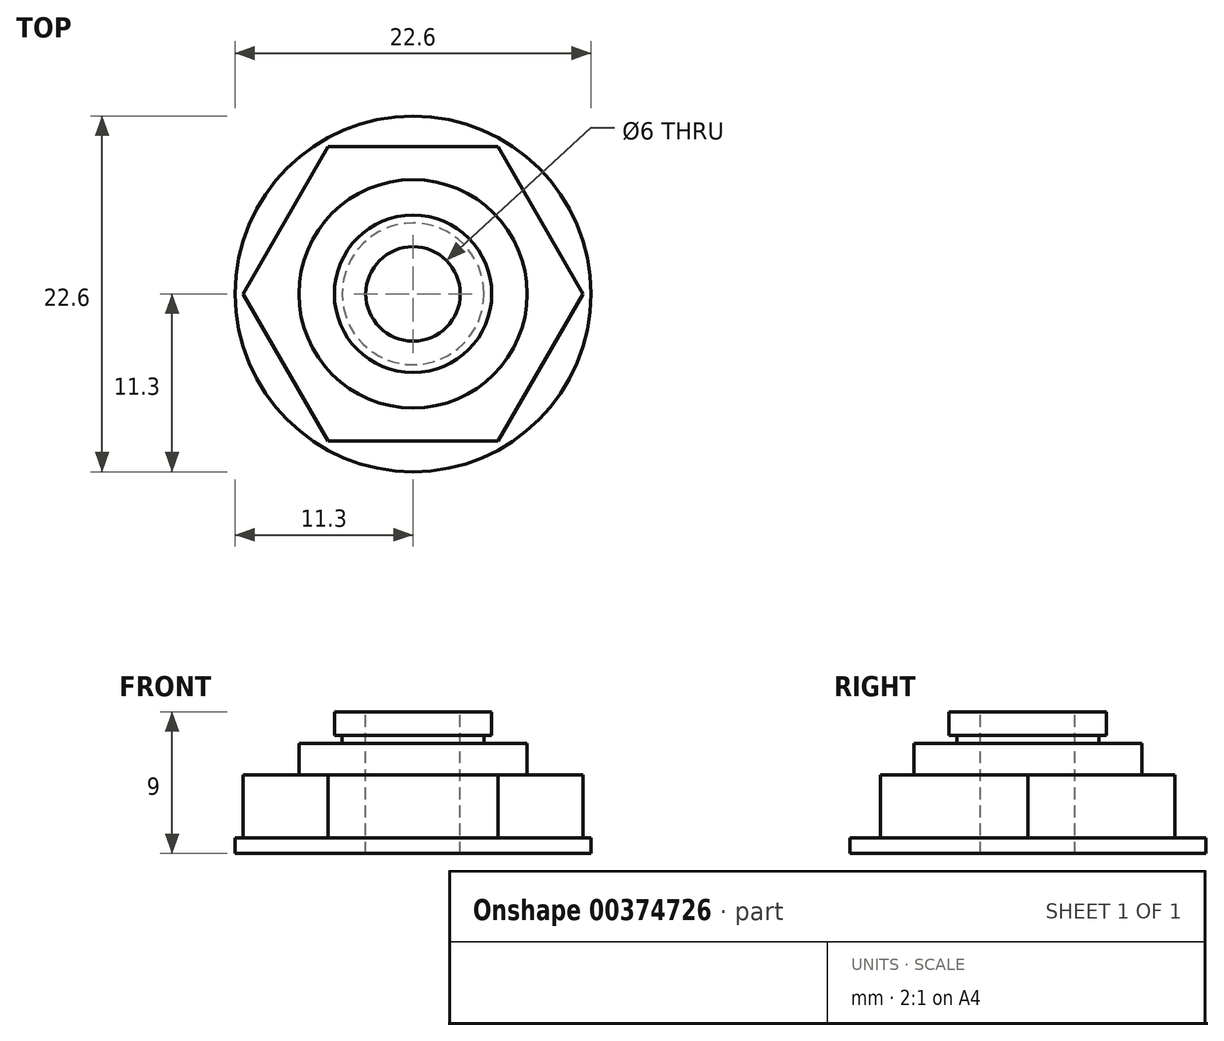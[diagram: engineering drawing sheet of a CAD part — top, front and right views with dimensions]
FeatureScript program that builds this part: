
annotation { "Feature Type Name" : "Feature", "Feature Type Description" : "" }
export const myFeature = defineFeature(function(context is Context, id is Id, definition is map)
    precondition{}
    {
        {
            var Q0;
            Q0=qCreatedBy(makeId("Top.planeOp"),FACE);
            var sketch = newSketch(context, id + "F0", { "sketchPlane" : qUnion([Q0])});
            skCircle(sketch, "E0", {"center": v(0, 0) * mm, "radius": 11.3 * mm});
            skCircle(sketch, "E1.cCircle", {"center": v(0, 0) * mm, "radius": 10.8 * mm, "construction": true});
            skLineSegment(sketch, "E1.0", {"start": v(5.4, -9.35) * mm, "end": v(-5.4, -9.35) * mm});
            skLineSegment(sketch, "E1.1", {"start": v(-5.4, -9.35) * mm, "end": v(-10.8, 0) * mm});
            skLineSegment(sketch, "E1.2", {"start": v(-10.8, 0) * mm, "end": v(-5.4, 9.35) * mm});
            skLineSegment(sketch, "E1.3", {"start": v(-5.4, 9.35) * mm, "end": v(5.4, 9.35) * mm});
            skLineSegment(sketch, "E1.4", {"start": v(5.4, 9.35) * mm, "end": v(10.8, 0) * mm});
            skLineSegment(sketch, "E1.5", {"start": v(10.8, 0) * mm, "end": v(5.4, -9.35) * mm});
            skSolve(sketch);
        }
        {
            var Q0;
            Q0=makeQuery(id+"F0.imprint","IMPRINT",FACE,{"disambiguationData":[TD([[makeQuery(id+"F0.imprint","IMPRINT",EDGE,{"derivedFrom":sQuery(id+"F0.wireOp",EDGE,"E0")}),1.0]])]});
            var Q1;
            Q1=makeQuery(id+"F0.imprint","IMPRINT",FACE,{"disambiguationData":[TD([[makeQuery(id+"F0.imprint","IMPRINT",EDGE,{"derivedFrom":sQuery(id+"F0.wireOp",EDGE,"E1.0")}),-1.0]])]});
            extrude(context, id + "F1", {"entities" : qUnion([Q0, Q1]), "depth" : 1 * mm});
        }
        {
            var Q0;
            Q0=makeQuery(id+"F0.imprint","IMPRINT",FACE,{"disambiguationData":[TD([[makeQuery(id+"F0.imprint","IMPRINT",EDGE,{"derivedFrom":sQuery(id+"F0.wireOp",EDGE,"E1.0")}),-1.0]])]});
            extrude(context, id + "F2", {"entities" : qUnion([Q0]), "operationType" : NewBodyOperationType.ADD, "depth" : 5 * mm});
        }
        {
            var Q0;
            Q0=makeQuery(id+"F2.opExtrude","CAP_FACE",FACE,{"disambiguationData":[OSD([sQuery(id+"F0.wireOp",EDGE,"E1.0"),sQuery(id+"F0.wireOp",EDGE,"E1.1"),sQuery(id+"F0.wireOp",EDGE,"E1.2"),sQuery(id+"F0.wireOp",EDGE,"E1.3"),sQuery(id+"F0.wireOp",EDGE,"E1.4"),sQuery(id+"F0.wireOp",EDGE,"E1.5")])],"isStart":false});
            var sketch = newSketch(context, id + "F3", { "sketchPlane" : qUnion([Q0])});
            skCircle(sketch, "E2", {"center": v(0, 0) * mm, "radius": 7.25 * mm});
            skSolve(sketch);
        }
        {
            var Q0;
            Q0 = qSketchRegion(id + "F3", true);
            extrude(context, id + "F4", {"entities" : qUnion([Q0]), "operationType" : NewBodyOperationType.ADD, "depth" : 2 * mm});
        }
        {
            var Q0;
            Q0=makeQuery(id+"F4.opExtrude","CAP_FACE",FACE,{"disambiguationData":[OSD([sQuery(id+"F3.wireOp",EDGE,"E2")])],"isStart":false});
            var sketch = newSketch(context, id + "F5", { "sketchPlane" : qUnion([Q0])});
            skCircle(sketch, "E3", {"center": v(0, 0) * mm, "radius": 4.5 * mm});
            skSolve(sketch);
        }
        {
            var Q0;
            Q0 = qSketchRegion(id + "F5", true);
            extrude(context, id + "F6", {"entities" : qUnion([Q0]), "operationType" : NewBodyOperationType.ADD, "depth" : .5 * mm});
        }
        {
            var Q0;
            Q0=makeQuery(id+"F6.opExtrude","CAP_FACE",FACE,{"disambiguationData":[OSD([sQuery(id+"F5.wireOp",EDGE,"E3")])],"isStart":false});
            var sketch = newSketch(context, id + "F7", { "sketchPlane" : qUnion([Q0])});
            skCircle(sketch, "E4", {"center": v(0, 0) * mm, "radius": 5 * mm});
            skSolve(sketch);
        }
        {
            var Q0;
            Q0 = qSketchRegion(id + "F7", true);
            extrude(context, id + "F8", {"entities" : qUnion([Q0]), "operationType" : NewBodyOperationType.ADD, "depth" : 1.5 * mm});
        }
        {
            var Q0;
            Q0=makeQuery(id+"F8.opExtrude","CAP_FACE",FACE,{"disambiguationData":[OSD([sQuery(id+"F7.wireOp",EDGE,"E4")])],"isStart":false});
            var sketch = newSketch(context, id + "F9", { "sketchPlane" : qUnion([Q0])});
            skCircle(sketch, "E5", {"center": v(0, 0) * mm, "radius": 3 * mm});
            skSolve(sketch);
        }
        {
            var Q0;
            Q0 = qSketchRegion(id + "F9", true);
            extrude(context, id + "F10", {"entities" : qUnion([Q0]), "operationType" : NewBodyOperationType.REMOVE, "oppositeDirection" : true, "depth" : 13.7 * mm});
        }
    });
